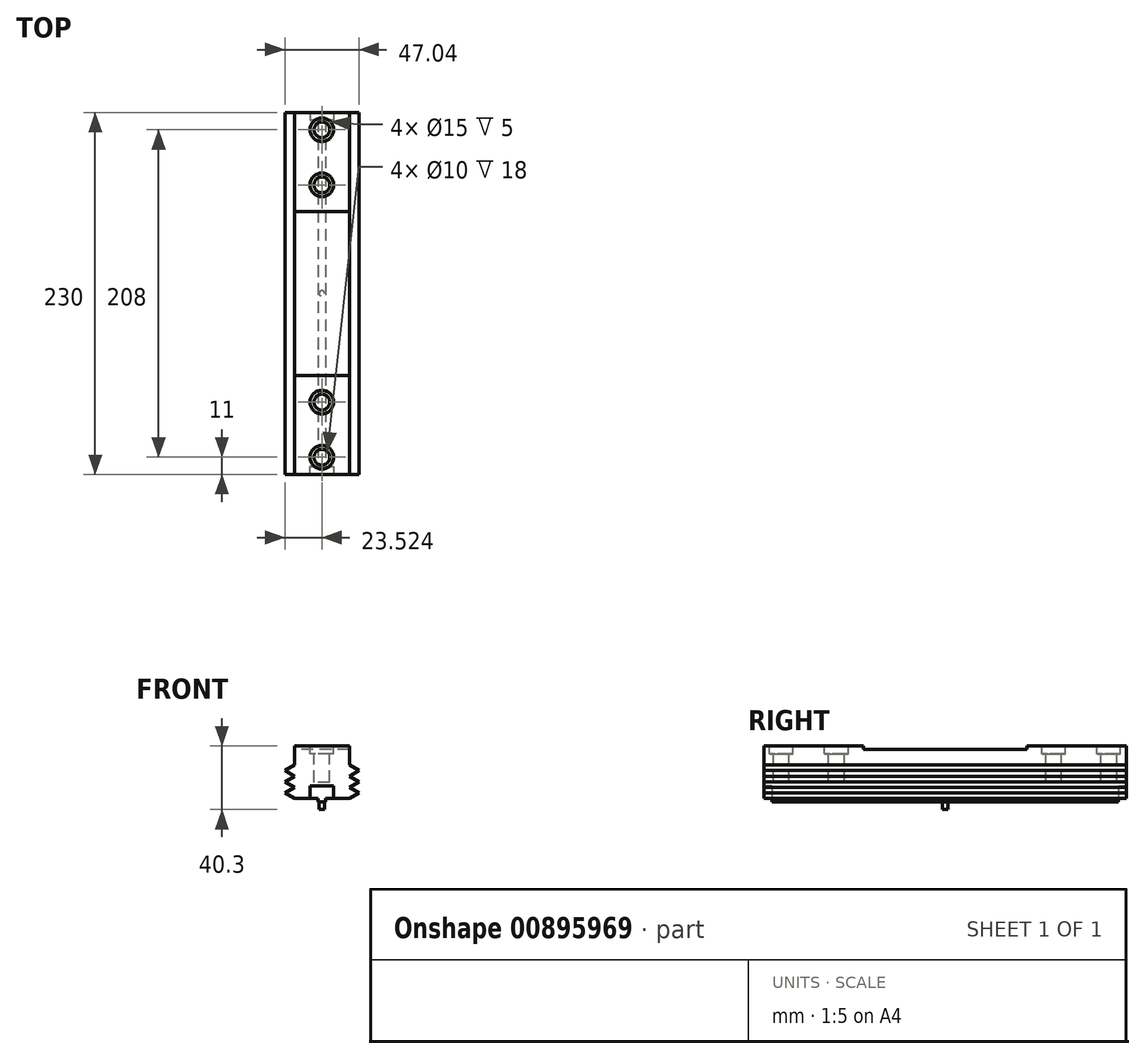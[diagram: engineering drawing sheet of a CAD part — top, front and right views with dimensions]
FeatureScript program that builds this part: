
annotation { "Feature Type Name" : "Feature", "Feature Type Description" : "" }
export const myFeature = defineFeature(function(context is Context, id is Id, definition is map)
    precondition{}
    {
        {
            var Q0;
            Q0=qCreatedBy(makeId("Top.planeOp"),FACE);
            var sketch = newSketch(context, id + "F0", { "sketchPlane" : qUnion([Q0])});
            skLineSegment(sketch, "E0.bottom", {"start": v(-17.99, 0) * mm, "end": v(17.01, 0) * mm});
            skLineSegment(sketch, "E0.top", {"start": v(-17.99, -63) * mm, "end": v(17.01, -63) * mm});
            skLineSegment(sketch, "E0.left", {"start": v(-17.99, 0) * mm, "end": v(-17.99, -63) * mm});
            skLineSegment(sketch, "E0.right", {"start": v(17.01, 0) * mm, "end": v(17.01, -63) * mm});
            skSolve(sketch);
        }
        {
            var Q0;
            Q0=makeQuery(id+"F0.imprint","IMPRINT",FACE,{"disambiguationData":[TD([[makeQuery(id+"F0.imprint","IMPRINT",EDGE,{"derivedFrom":sQuery(id+"F0.wireOp",EDGE,"E0.bottom")}),-1.0]])]});
            extrude(context, id + "F1", {"entities" : qUnion([Q0]), "oppositeDirection" : true, "depth" : 35.3 * mm, "offsetDistance" : 25 * mm});
        }
        {
            var Q0;
            Q0=makeQuery(id+"F1.opExtrude","SWEPT_FACE",FACE,{"disambiguationData":[OSD([sQuery(id+"F0.wireOp",EDGE,"E0.top")])]});
            var sketch = newSketch(context, id + "F2", { "sketchPlane" : qUnion([Q0])});
            skLineSegment(sketch, "E1", {"start": v(-17.99, -12) * mm, "end": v(-24, -15.55) * mm});
            skLineSegment(sketch, "E2", {"start": v(-24, -15.55) * mm, "end": v(-17.99, -19.1) * mm});
            skLineSegment(sketch, "E3", {"start": v(-17.99, -19.1) * mm, "end": v(-24, -22.65) * mm});
            skLineSegment(sketch, "E4", {"start": v(-24, -22.65) * mm, "end": v(-17.99, -26.2) * mm});
            skLineSegment(sketch, "E5", {"start": v(-17.99, -26.2) * mm, "end": v(-24, -29.75) * mm});
            skLineSegment(sketch, "E6", {"start": v(-24, -29.75) * mm, "end": v(-17.99, -33.3) * mm});
            skLineSegment(sketch, "E7", {"start": v(17.01, -33.3) * mm, "end": v(23.03, -29.75) * mm});
            skLineSegment(sketch, "E8", {"start": v(23.03, -29.75) * mm, "end": v(17.01, -26.2) * mm});
            skLineSegment(sketch, "E9", {"start": v(17.01, -26.2) * mm, "end": v(23.03, -22.65) * mm});
            skLineSegment(sketch, "E10", {"start": v(23.03, -22.65) * mm, "end": v(17.01, -19.1) * mm});
            skLineSegment(sketch, "E11", {"start": v(17.01, -19.1) * mm, "end": v(23.03, -15.55) * mm});
            skLineSegment(sketch, "E12", {"start": v(23.03, -15.55) * mm, "end": v(17.01, -12) * mm});
            skLineSegment(sketch, "E13", {"start": v(-17.99, -33.3) * mm, "end": v(-2.99, -33.3) * mm});
            skLineSegment(sketch, "E14", {"start": v(17.01, -33.3) * mm, "end": v(2.01, -33.3) * mm});
            skLineSegment(sketch, "E15", {"start": v(-2.99, -33.3) * mm, "end": v(-2.99, -35.3) * mm});
            skLineSegment(sketch, "E16", {"start": v(2.01, -33.3) * mm, "end": v(2.01, -35.3) * mm});
            skLineSegment(sketch, "E17", {"start": v(2.01, -35.3) * mm, "end": v(-2.99, -35.3) * mm});
            skLineSegment(sketch, "E18", {"start": v(-17.99, 0) * mm, "end": v(-17.99, -12) * mm});
            skLineSegment(sketch, "E19", {"start": v(17.01, 0) * mm, "end": v(17.01, -12) * mm});
            skSolve(sketch);
        }
        {
            var Q0;
            Q0 = qSketchRegion(id + "F2", true);
            var Q1;
            {var subQ0=sQuery(id+"F2.wireOp",EDGE,"E14");Q1=makeQuery(id+"F2.imprint","IMPRINT",FACE,{"disambiguationData":[TD([[makeQuery(id+"F2.imprint","IMPRINT",EDGE,{"derivedFrom":subQ0}),1.0]])]});}
            var Q2;
            {var subQ0=sQuery(id+"F2.wireOp",EDGE,"E13");Q2=makeQuery(id+"F2.imprint","IMPRINT",FACE,{"disambiguationData":[TD([[makeQuery(id+"F2.imprint","IMPRINT",EDGE,{"derivedFrom":subQ0}),-1.0]])]});}
            extrude(context, id + "F3", {"entities" : qUnion([Q0, Q1, Q2]), "operationType" : NewBodyOperationType.REMOVE, "endBound" : BoundingType.THROUGH_ALL, "oppositeDirection" : true, "depth" : 25 * mm, "offsetDistance" : 25 * mm});
        }
        {
            var Q0;
            {var subQ0=sQuery(id+"F2.wireOp",EDGE,"E1");Q0=makeQuery(id+"F2.imprint","IMPRINT",FACE,{"disambiguationData":[TD([[makeQuery(id+"F2.imprint","IMPRINT",EDGE,{"derivedFrom":subQ0}),1.0]])]});}
            var Q1;
            {var subQ0=sQuery(id+"F2.wireOp",EDGE,"E3");Q1=makeQuery(id+"F2.imprint","IMPRINT",FACE,{"disambiguationData":[TD([[makeQuery(id+"F2.imprint","IMPRINT",EDGE,{"derivedFrom":subQ0}),1.0]])]});}
            var Q2;
            {var subQ0=sQuery(id+"F2.wireOp",EDGE,"E5");Q2=makeQuery(id+"F2.imprint","IMPRINT",FACE,{"disambiguationData":[TD([[makeQuery(id+"F2.imprint","IMPRINT",EDGE,{"derivedFrom":subQ0}),1.0]])]});}
            var Q3;
            {var subQ0=sQuery(id+"F2.wireOp",EDGE,"E7");Q3=makeQuery(id+"F2.imprint","IMPRINT",FACE,{"disambiguationData":[TD([[makeQuery(id+"F2.imprint","IMPRINT",EDGE,{"derivedFrom":subQ0}),1.0]])]});}
            var Q4;
            {var subQ0=sQuery(id+"F2.wireOp",EDGE,"E11");Q4=makeQuery(id+"F2.imprint","IMPRINT",FACE,{"disambiguationData":[TD([[makeQuery(id+"F2.imprint","IMPRINT",EDGE,{"derivedFrom":subQ0}),1.0]])]});}
            var Q5;
            {var subQ0=sQuery(id+"F2.wireOp",EDGE,"E9");Q5=makeQuery(id+"F2.imprint","IMPRINT",FACE,{"disambiguationData":[TD([[makeQuery(id+"F2.imprint","IMPRINT",EDGE,{"derivedFrom":subQ0}),1.0]])]});}
            extrude(context, id + "F4", {"entities" : qUnion([Q0, Q1, Q2, Q3, Q4, Q5]), "operationType" : NewBodyOperationType.ADD, "oppositeDirection" : true, "depth" : 63 * mm, "offsetDistance" : 25 * mm});
        }
        {
            var Q0;
            Q0=makeQuery(id+"F1.opExtrude","CAP_FACE",FACE,{"disambiguationData":[OSD([sQuery(id+"F0.wireOp",EDGE,"E0.bottom"),sQuery(id+"F0.wireOp",EDGE,"E0.top"),sQuery(id+"F0.wireOp",EDGE,"E0.left"),sQuery(id+"F0.wireOp",EDGE,"E0.right")])],"isStart":true});
            var sketch = newSketch(context, id + "F5", { "sketchPlane" : qUnion([Q0])});
            skCircle(sketch, "E20", {"center": v(-0.49, -52) * mm, "radius": 5 * mm});
            skCircle(sketch, "E21", {"center": v(-0.49, -17) * mm, "radius": 5 * mm});
            skCircle(sketch, "E22", {"center": v(-0.49, -17) * mm, "radius": 7.5 * mm});
            skCircle(sketch, "E23", {"center": v(-0.49, -52) * mm, "radius": 7.5 * mm});
            skSolve(sketch);
        }
        {
            var Q0;
            Q0=makeQuery(id+"F5.imprint","IMPRINT",FACE,{"disambiguationData":[TD([[makeQuery(id+"F5.imprint","IMPRINT",EDGE,{"derivedFrom":sQuery(id+"F5.wireOp",EDGE,"E21")}),1.0]])]});
            var Q1;
            Q1=makeQuery(id+"F5.imprint","IMPRINT",FACE,{"disambiguationData":[TD([[makeQuery(id+"F5.imprint","IMPRINT",EDGE,{"derivedFrom":sQuery(id+"F5.wireOp",EDGE,"E20")}),1.0]])]});
            extrude(context, id + "F6", {"entities" : qUnion([Q0, Q1]), "operationType" : NewBodyOperationType.REMOVE, "oppositeDirection" : true, "depth" : 23 * mm, "offsetDistance" : 25 * mm});
        }
        {
            var Q0;
            Q0 = qSketchRegion(id + "F5", true);
            extrude(context, id + "F7", {"entities" : qUnion([Q0]), "operationType" : NewBodyOperationType.REMOVE, "oppositeDirection" : true, "depth" : 5 * mm, "offsetDistance" : 25 * mm});
        }
        {
            var Q0;
            {var subQ0=sQuery(id+"F0.wireOp",EDGE,"E0.right");var subQ1=sQuery(id+"F0.wireOp",EDGE,"E0.top");var subQ2=sQuery(id+"F0.wireOp",EDGE,"E0.left");Q0=makeQuery(id+"F4.boolean.opBoolean","MERGE",FACE,{"derivedFrom":[makeQuery(id+"F1.opExtrude","SWEPT_FACE",FACE,{"disambiguationData":[OSD([subQ1])]}),makeQuery(id+"F4.opExtrude","CAP_FACE",FACE,{"disambiguationData":[OSD([subQ1,subQ2,sQuery(id+"F2.wireOp",EDGE,"E1"),sQuery(id+"F2.wireOp",EDGE,"E2")])],"isStart":true}),makeQuery(id+"F4.opExtrude","CAP_FACE",FACE,{"disambiguationData":[OSD([subQ1,subQ2,sQuery(id+"F2.wireOp",EDGE,"E3"),sQuery(id+"F2.wireOp",EDGE,"E4")])],"isStart":true}),makeQuery(id+"F4.opExtrude","CAP_FACE",FACE,{"disambiguationData":[OSD([subQ1,subQ2,sQuery(id+"F2.wireOp",EDGE,"E5"),sQuery(id+"F2.wireOp",EDGE,"E6")])],"isStart":true}),makeQuery(id+"F4.opExtrude","CAP_FACE",FACE,{"disambiguationData":[OSD([subQ1,subQ0,sQuery(id+"F2.wireOp",EDGE,"E7"),sQuery(id+"F2.wireOp",EDGE,"E8")])],"isStart":true}),makeQuery(id+"F4.opExtrude","CAP_FACE",FACE,{"disambiguationData":[OSD([subQ1,subQ0,sQuery(id+"F2.wireOp",EDGE,"E9"),sQuery(id+"F2.wireOp",EDGE,"E10")])],"isStart":true}),makeQuery(id+"F4.opExtrude","CAP_FACE",FACE,{"disambiguationData":[OSD([subQ1,subQ0,sQuery(id+"F2.wireOp",EDGE,"E11"),sQuery(id+"F2.wireOp",EDGE,"E12")])],"isStart":true})]});}
            var sketch = newSketch(context, id + "F8", { "sketchPlane" : qUnion([Q0])});
            skLineSegment(sketch, "E24", {"start": v(-0.49, -35.3) * mm, "end": v(-0.49, -22.62) * mm});
            skLineSegment(sketch, "E25.bottom", {"start": v(-7.99, -25.3) * mm, "end": v(7.01, -25.3) * mm});
            skLineSegment(sketch, "E25.top", {"start": v(-7.99, -35.5) * mm, "end": v(7.01, -35.5) * mm});
            skLineSegment(sketch, "E25.left", {"start": v(-7.99, -25.3) * mm, "end": v(-7.99, -35.5) * mm});
            skLineSegment(sketch, "E25.right", {"start": v(7.01, -25.3) * mm, "end": v(7.01, -35.5) * mm});
            skSolve(sketch);
        }
        {
            var Q0;
            Q0 = qSketchRegion(id + "F8", true);
            extrude(context, id + "F9", {"entities" : qUnion([Q0]), "operationType" : NewBodyOperationType.REMOVE, "oppositeDirection" : true, "depth" : 5 * mm, "offsetDistance" : 25 * mm});
        }
        {
            var Q0;
            {var subQ0=sQuery(id+"F0.wireOp",EDGE,"E0.right");var subQ1=sQuery(id+"F0.wireOp",EDGE,"E0.top");var subQ2=sQuery(id+"F0.wireOp",EDGE,"E0.left");Q0=makeQuery(id+"F4.boolean.opBoolean","MERGE",FACE,{"derivedFrom":[makeQuery(id+"F1.opExtrude","SWEPT_FACE",FACE,{"disambiguationData":[OSD([sQuery(id+"F0.wireOp",EDGE,"E0.bottom")])]}),makeQuery(id+"F4.opExtrude","CAP_FACE",FACE,{"disambiguationData":[OSD([subQ1,subQ2,sQuery(id+"F2.wireOp",EDGE,"E1"),sQuery(id+"F2.wireOp",EDGE,"E2")])],"isStart":false}),makeQuery(id+"F4.opExtrude","CAP_FACE",FACE,{"disambiguationData":[OSD([subQ1,subQ2,sQuery(id+"F2.wireOp",EDGE,"E3"),sQuery(id+"F2.wireOp",EDGE,"E4")])],"isStart":false}),makeQuery(id+"F4.opExtrude","CAP_FACE",FACE,{"disambiguationData":[OSD([subQ1,subQ2,sQuery(id+"F2.wireOp",EDGE,"E5"),sQuery(id+"F2.wireOp",EDGE,"E6")])],"isStart":false}),makeQuery(id+"F4.opExtrude","CAP_FACE",FACE,{"disambiguationData":[OSD([subQ1,subQ0,sQuery(id+"F2.wireOp",EDGE,"E7"),sQuery(id+"F2.wireOp",EDGE,"E8")])],"isStart":false}),makeQuery(id+"F4.opExtrude","CAP_FACE",FACE,{"disambiguationData":[OSD([subQ1,subQ0,sQuery(id+"F2.wireOp",EDGE,"E9"),sQuery(id+"F2.wireOp",EDGE,"E10")])],"isStart":false}),makeQuery(id+"F4.opExtrude","CAP_FACE",FACE,{"disambiguationData":[OSD([subQ1,subQ0,sQuery(id+"F2.wireOp",EDGE,"E11"),sQuery(id+"F2.wireOp",EDGE,"E12")])],"isStart":false})]});}
            var sketch = newSketch(context, id + "F10", { "sketchPlane" : qUnion([Q0])});
            skLineSegment(sketch, "E26.bottom", {"start": v(-17.01, -2) * mm, "end": v(17.99, -2) * mm});
            skLineSegment(sketch, "E26.left", {"start": v(-17.01, -2) * mm, "end": v(-17.01, -12) * mm});
            skLineSegment(sketch, "E26.right", {"start": v(17.99, -2) * mm, "end": v(17.99, -12) * mm});
            skLineSegment(sketch, "E27", {"start": v(-17.01, -12) * mm, "end": v(-23.03, -15.55) * mm});
            skLineSegment(sketch, "E28", {"start": v(-23.03, -15.55) * mm, "end": v(-17.01, -19.1) * mm});
            skLineSegment(sketch, "E29", {"start": v(-17.01, -19.1) * mm, "end": v(-23.03, -22.65) * mm});
            skLineSegment(sketch, "E30", {"start": v(-23.03, -22.65) * mm, "end": v(-17.01, -26.2) * mm});
            skLineSegment(sketch, "E31", {"start": v(-17.01, -26.2) * mm, "end": v(-23.03, -29.75) * mm});
            skLineSegment(sketch, "E32", {"start": v(-23.03, -29.75) * mm, "end": v(-17.01, -33.3) * mm});
            skLineSegment(sketch, "E33", {"start": v(-17.01, -33.3) * mm, "end": v(-2.01, -33.3) * mm});
            skLineSegment(sketch, "E34", {"start": v(-2.01, -33.3) * mm, "end": v(-2.01, -35.3) * mm});
            skLineSegment(sketch, "E35", {"start": v(-2.01, -35.3) * mm, "end": v(2.99, -35.3) * mm});
            skLineSegment(sketch, "E36", {"start": v(2.99, -35.3) * mm, "end": v(2.99, -33.3) * mm});
            skLineSegment(sketch, "E37", {"start": v(2.99, -33.3) * mm, "end": v(17.99, -33.3) * mm});
            skLineSegment(sketch, "E38", {"start": v(17.99, -33.3) * mm, "end": v(24, -29.75) * mm});
            skLineSegment(sketch, "E39", {"start": v(24, -29.75) * mm, "end": v(17.99, -26.2) * mm});
            skLineSegment(sketch, "E40", {"start": v(17.99, -26.2) * mm, "end": v(24, -22.65) * mm});
            skLineSegment(sketch, "E41", {"start": v(24, -22.65) * mm, "end": v(17.99, -19.1) * mm});
            skLineSegment(sketch, "E42", {"start": v(17.99, -19.1) * mm, "end": v(24, -15.55) * mm});
            skLineSegment(sketch, "E43", {"start": v(24, -15.55) * mm, "end": v(17.99, -12) * mm});
            skSolve(sketch);
        }
        {
            var Q0;
            Q0 = qSketchRegion(id + "F10", true);
            var Q1;
            Q1=makeQuery(id+"F10.imprint","IMPRINT",FACE,{"disambiguationData":[TD([[makeQuery(id+"F10.imprint","IMPRINT",EDGE,{"derivedFrom":sQuery(id+"F10.wireOp",EDGE,"E26.bottom")}),-1.0]])]});
            extrude(context, id + "F11", {"entities" : qUnion([Q0, Q1]), "operationType" : NewBodyOperationType.ADD, "depth" : 104 * mm, "offsetDistance" : 25 * mm});
        }
        {
            var Q0;
            Q0=makeQuery(id+"F11.opExtrude","CAP_FACE",FACE,{"disambiguationData":[OSD([sQuery(id+"F10.wireOp",EDGE,"E26.bottom"),sQuery(id+"F10.wireOp",EDGE,"E26.left"),sQuery(id+"F10.wireOp",EDGE,"E26.right"),sQuery(id+"F10.wireOp",EDGE,"E27"),sQuery(id+"F10.wireOp",EDGE,"E28"),sQuery(id+"F10.wireOp",EDGE,"E29"),sQuery(id+"F10.wireOp",EDGE,"E30"),sQuery(id+"F10.wireOp",EDGE,"E31"),sQuery(id+"F10.wireOp",EDGE,"E32"),sQuery(id+"F10.wireOp",EDGE,"E33"),sQuery(id+"F10.wireOp",EDGE,"E34"),sQuery(id+"F10.wireOp",EDGE,"E35"),sQuery(id+"F10.wireOp",EDGE,"E36"),sQuery(id+"F10.wireOp",EDGE,"E37"),sQuery(id+"F10.wireOp",EDGE,"E38"),sQuery(id+"F10.wireOp",EDGE,"E39"),sQuery(id+"F10.wireOp",EDGE,"E40"),sQuery(id+"F10.wireOp",EDGE,"E41"),sQuery(id+"F10.wireOp",EDGE,"E42"),sQuery(id+"F10.wireOp",EDGE,"E43")])],"isStart":false});
            var sketch = newSketch(context, id + "F12", { "sketchPlane" : qUnion([Q0])});
            skLineSegment(sketch, "E44.bottom", {"start": v(-17.01, 0) * mm, "end": v(17.99, 0) * mm});
            skLineSegment(sketch, "E45", {"start": v(-17.01, 0) * mm, "end": v(-17.01, -12) * mm});
            skLineSegment(sketch, "E46", {"start": v(-17.01, -12) * mm, "end": v(-23.03, -15.55) * mm});
            skLineSegment(sketch, "E47", {"start": v(-23.03, -15.55) * mm, "end": v(-17.01, -19.1) * mm});
            skLineSegment(sketch, "E48", {"start": v(-17.01, -19.1) * mm, "end": v(-23.03, -22.65) * mm});
            skLineSegment(sketch, "E49", {"start": v(-23.03, -22.65) * mm, "end": v(-17.01, -26.2) * mm});
            skLineSegment(sketch, "E50", {"start": v(-17.01, -26.2) * mm, "end": v(-23.03, -29.75) * mm});
            skLineSegment(sketch, "E51", {"start": v(-23.03, -29.75) * mm, "end": v(-17.01, -33.3) * mm});
            skLineSegment(sketch, "E52", {"start": v(-17.01, -33.3) * mm, "end": v(-2.01, -33.3) * mm});
            skLineSegment(sketch, "E53", {"start": v(-2.01, -33.3) * mm, "end": v(-2.01, -35.3) * mm});
            skLineSegment(sketch, "E54", {"start": v(-2.01, -35.3) * mm, "end": v(2.99, -35.3) * mm});
            skLineSegment(sketch, "E55", {"start": v(2.99, -35.3) * mm, "end": v(2.99, -33.3) * mm});
            skLineSegment(sketch, "E56", {"start": v(2.99, -33.3) * mm, "end": v(17.99, -33.3) * mm});
            skLineSegment(sketch, "E57", {"start": v(17.99, -33.3) * mm, "end": v(24, -29.75) * mm});
            skLineSegment(sketch, "E58", {"start": v(24, -29.75) * mm, "end": v(17.99, -26.2) * mm});
            skLineSegment(sketch, "E59", {"start": v(17.99, -26.2) * mm, "end": v(24, -22.65) * mm});
            skLineSegment(sketch, "E60", {"start": v(24, -22.65) * mm, "end": v(17.99, -19.1) * mm});
            skLineSegment(sketch, "E61", {"start": v(17.99, -19.1) * mm, "end": v(24, -15.55) * mm});
            skLineSegment(sketch, "E62", {"start": v(24, -15.55) * mm, "end": v(17.99, -12) * mm});
            skLineSegment(sketch, "E63", {"start": v(17.99, -12) * mm, "end": v(17.99, 0) * mm});
            skSolve(sketch);
        }
        {
            var Q0;
            Q0 = qSketchRegion(id + "F12", true);
            extrude(context, id + "F13", {"entities" : qUnion([Q0]), "operationType" : NewBodyOperationType.ADD, "depth" : 63 * mm, "offsetDistance" : 25 * mm});
        }
        {
            var Q0;
            Q0=makeQuery(id+"F13.opExtrude","SWEPT_FACE",FACE,{"disambiguationData":[OSD([sQuery(id+"F12.wireOp",EDGE,"E44.bottom")])]});
            var sketch = newSketch(context, id + "F14", { "sketchPlane" : qUnion([Q0])});
            skCircle(sketch, "E64", {"center": v(-0.49, 121) * mm, "radius": 5 * mm});
            skCircle(sketch, "E65", {"center": v(-0.49, 156) * mm, "radius": 5 * mm});
            skCircle(sketch, "E66", {"center": v(-0.49, 156) * mm, "radius": 7.5 * mm});
            skCircle(sketch, "E67", {"center": v(-0.49, 121) * mm, "radius": 7.5 * mm});
            skSolve(sketch);
        }
        {
            var Q0;
            Q0=makeQuery(id+"F14.imprint","IMPRINT",FACE,{"disambiguationData":[TD([[makeQuery(id+"F14.imprint","IMPRINT",EDGE,{"derivedFrom":sQuery(id+"F14.wireOp",EDGE,"E65")}),1.0]])]});
            var Q1;
            Q1=makeQuery(id+"F14.imprint","IMPRINT",FACE,{"disambiguationData":[TD([[makeQuery(id+"F14.imprint","IMPRINT",EDGE,{"derivedFrom":sQuery(id+"F14.wireOp",EDGE,"E64")}),1.0]])]});
            extrude(context, id + "F15", {"entities" : qUnion([Q0, Q1]), "operationType" : NewBodyOperationType.REMOVE, "oppositeDirection" : true, "depth" : 23 * mm, "offsetDistance" : 25 * mm});
        }
        {
            var Q0;
            Q0 = qSketchRegion(id + "F14", true);
            extrude(context, id + "F16", {"entities" : qUnion([Q0]), "operationType" : NewBodyOperationType.REMOVE, "oppositeDirection" : true, "depth" : 5 * mm, "offsetDistance" : 25 * mm});
        }
        {
            var Q0;
            Q0=makeQuery(id+"F13.boolean.opBoolean","MERGE",FACE,{"derivedFrom":[makeQuery(id+"F11.boolean.opBoolean","MERGE",FACE,{"derivedFrom":[makeQuery(id+"F1.opExtrude","CAP_FACE",FACE,{"disambiguationData":[OSD([sQuery(id+"F0.wireOp",EDGE,"E0.bottom"),sQuery(id+"F0.wireOp",EDGE,"E0.top"),sQuery(id+"F0.wireOp",EDGE,"E0.left"),sQuery(id+"F0.wireOp",EDGE,"E0.right")])],"isStart":false}),makeQuery(id+"F11.opExtrude","SWEPT_FACE",FACE,{"disambiguationData":[OSD([sQuery(id+"F10.wireOp",EDGE,"E35")])]})]}),makeQuery(id+"F13.opExtrude","SWEPT_FACE",FACE,{"disambiguationData":[OSD([sQuery(id+"F12.wireOp",EDGE,"E54")])]})]});
            var sketch = newSketch(context, id + "F17", { "sketchPlane" : qUnion([Q0])});
            skCircle(sketch, "E68", {"center": v(-0.49, -52) * mm, "radius": 1.75 * mm});
            skSolve(sketch);
        }
        {
            var Q0;
            Q0 = qSketchRegion(id + "F17", true);
            extrude(context, id + "F18", {"entities" : qUnion([Q0]), "operationType" : NewBodyOperationType.ADD, "depth" : 5 * mm, "offsetDistance" : 25 * mm});
        }
        {
            var Q0;
            Q0=makeQuery(id+"F13.opExtrude","CAP_FACE",FACE,{"disambiguationData":[OSD([sQuery(id+"F12.wireOp",EDGE,"E44.bottom"),sQuery(id+"F12.wireOp",EDGE,"E45"),sQuery(id+"F12.wireOp",EDGE,"E46"),sQuery(id+"F12.wireOp",EDGE,"E47"),sQuery(id+"F12.wireOp",EDGE,"E48"),sQuery(id+"F12.wireOp",EDGE,"E49"),sQuery(id+"F12.wireOp",EDGE,"E50"),sQuery(id+"F12.wireOp",EDGE,"E51"),sQuery(id+"F12.wireOp",EDGE,"E52"),sQuery(id+"F12.wireOp",EDGE,"E53"),sQuery(id+"F12.wireOp",EDGE,"E54"),sQuery(id+"F12.wireOp",EDGE,"E55"),sQuery(id+"F12.wireOp",EDGE,"E56"),sQuery(id+"F12.wireOp",EDGE,"E57"),sQuery(id+"F12.wireOp",EDGE,"E58"),sQuery(id+"F12.wireOp",EDGE,"E59"),sQuery(id+"F12.wireOp",EDGE,"E60"),sQuery(id+"F12.wireOp",EDGE,"E61"),sQuery(id+"F12.wireOp",EDGE,"E62"),sQuery(id+"F12.wireOp",EDGE,"E63")])],"isStart":false});
            var sketch = newSketch(context, id + "F19", { "sketchPlane" : qUnion([Q0])});
            skLineSegment(sketch, "E69", {"start": v(0.49, -25.3) * mm, "end": v(7.99, -25.3) * mm});
            skLineSegment(sketch, "E70", {"start": v(7.99, -25.3) * mm, "end": v(7.99, -35.3) * mm});
            skLineSegment(sketch, "E71", {"start": v(7.99, -35.3) * mm, "end": v(0.49, -35.3) * mm});
            skLineSegment(sketch, "E72", {"start": v(-7.01, -35.3) * mm, "end": v(0.49, -35.3) * mm});
            skLineSegment(sketch, "E73", {"start": v(-7.01, -35.3) * mm, "end": v(-7.01, -25.3) * mm});
            skLineSegment(sketch, "E74", {"start": v(-7.01, -25.3) * mm, "end": v(0.49, -25.3) * mm});
            skSolve(sketch);
        }
        {
            var Q0;
            Q0 = qSketchRegion(id + "F19", true);
            extrude(context, id + "F20", {"entities" : qUnion([Q0]), "operationType" : NewBodyOperationType.REMOVE, "oppositeDirection" : true, "depth" : 5 * mm, "offsetDistance" : 25 * mm});
        }
    });
